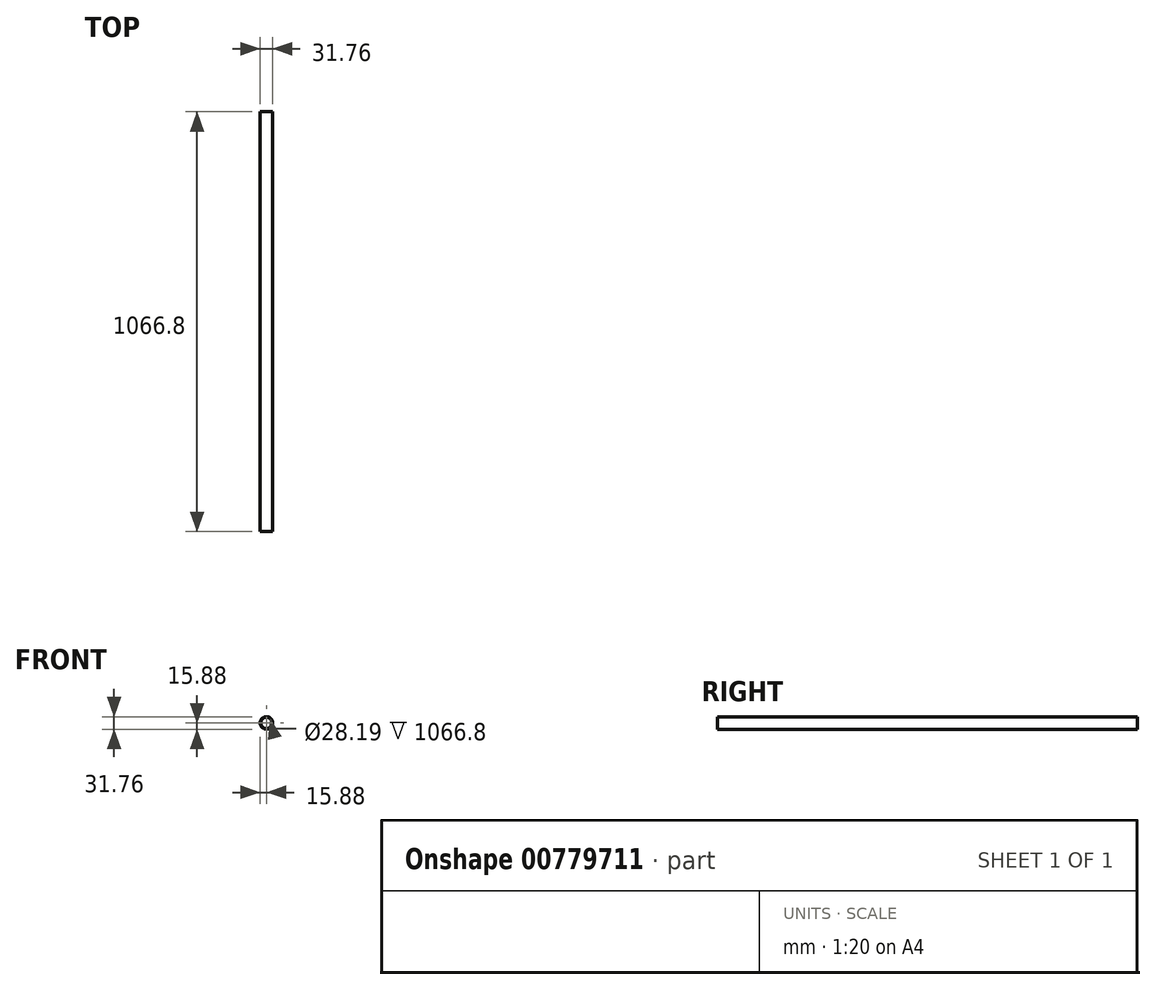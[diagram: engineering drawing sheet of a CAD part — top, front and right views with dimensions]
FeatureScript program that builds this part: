
annotation { "Feature Type Name" : "Feature", "Feature Type Description" : "" }
export const myFeature = defineFeature(function(context is Context, id is Id, definition is map)
    precondition{}
    {
        {
            var Q0;
            Q0=qCreatedBy(makeId("Front.planeOp"),FACE);
            var sketch = newSketch(context, id + "F0", { "sketchPlane" : qUnion([Q0])});
            skCircle(sketch, "E0", {"center": v(0, 0) * mm, "radius": 15.88 * mm});
            skCircle(sketch, "E1", {"center": v(0, 0) * mm, "radius": 14.1 * mm});
            skSolve(sketch);
        }
        {
            var Q0;
            Q0=makeQuery(id+"F0.imprint","IMPRINT",FACE,{"disambiguationData":[TD([[makeQuery(id+"F0.imprint","IMPRINT",EDGE,{"derivedFrom":sQuery(id+"F0.wireOp",EDGE,"E0")}),1.0]])]});
            extrude(context, id + "F1", {"entities" : qUnion([Q0]), "endBound" : BoundingType.SYMMETRIC, "depth" : 1066.8 * mm, "offsetDistance" : 25.4 * mm});
        }
    });
